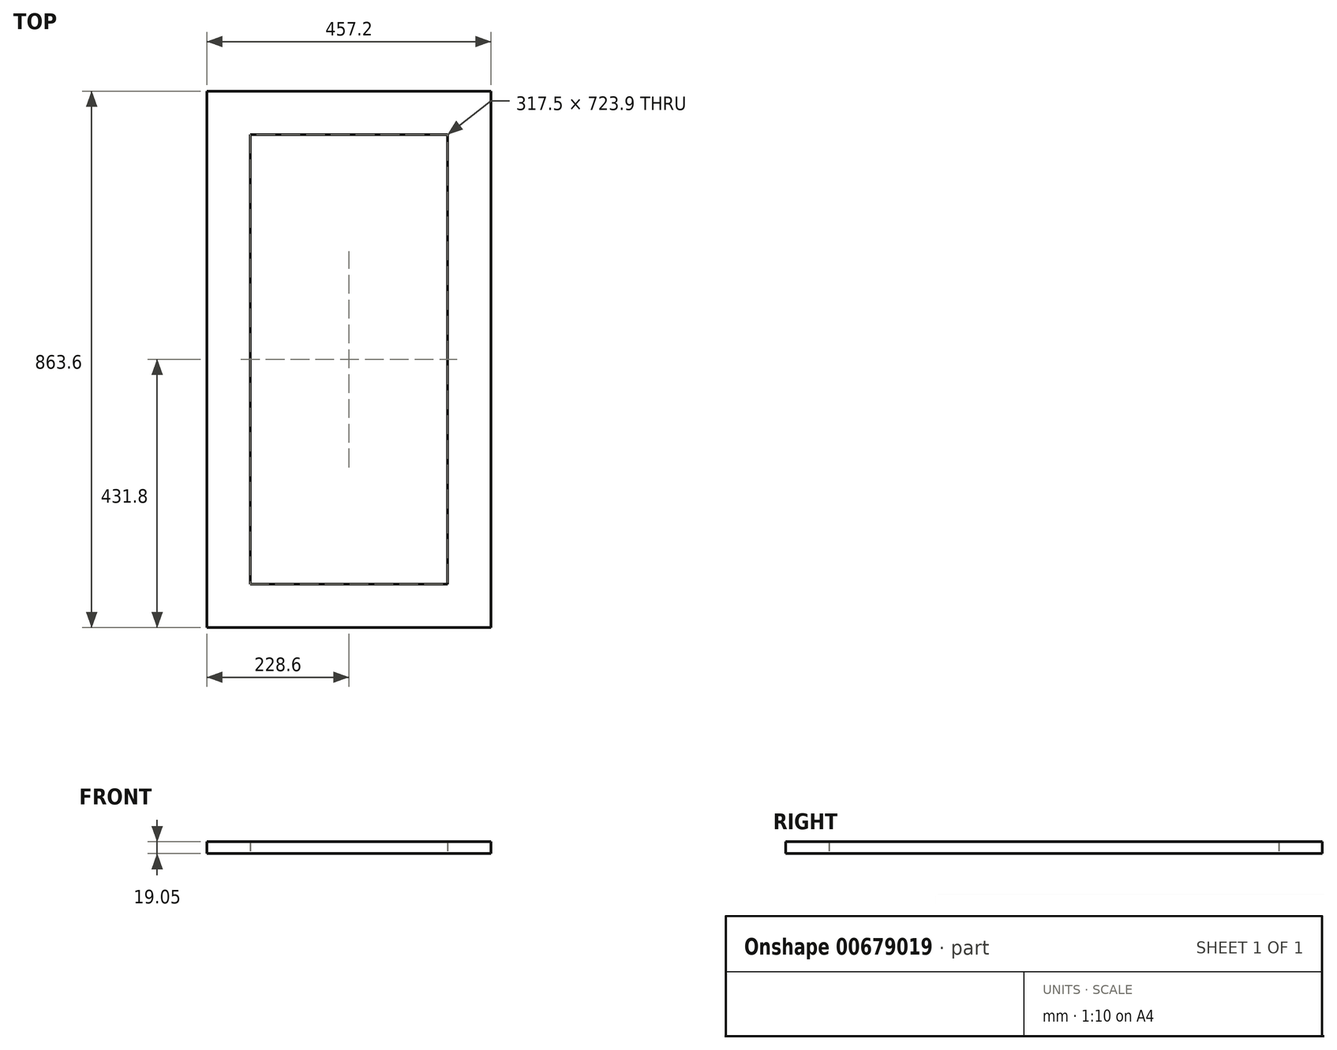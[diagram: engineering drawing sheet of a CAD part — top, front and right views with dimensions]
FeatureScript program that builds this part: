
annotation { "Feature Type Name" : "Feature", "Feature Type Description" : "" }
export const myFeature = defineFeature(function(context is Context, id is Id, definition is map)
    precondition{}
    {
        {
            var Q0;
            Q0=qCreatedBy(makeId("Top.planeOp"),FACE);
            var sketch = newSketch(context, id + "F0", { "sketchPlane" : qUnion([Q0])});
            skLineSegment(sketch, "E0.bottom", {"start": v(228.6, 431.8) * mm, "end": v(-228.6, 431.8) * mm});
            skLineSegment(sketch, "E0.top", {"start": v(228.6, -431.8) * mm, "end": v(-228.6, -431.8) * mm});
            skLineSegment(sketch, "E0.left", {"start": v(228.6, 431.8) * mm, "end": v(228.6, -431.8) * mm});
            skLineSegment(sketch, "E0.right", {"start": v(-228.6, 431.8) * mm, "end": v(-228.6, -431.8) * mm});
            skPoint(sketch, "E0.middle", {"position": v(0, 0) * mm});
            skLineSegment(sketch, "E1.bottom", {"start": v(158.75, 361.95) * mm, "end": v(-158.75, 361.95) * mm});
            skLineSegment(sketch, "E1.top", {"start": v(158.75, -361.95) * mm, "end": v(-158.75, -361.95) * mm});
            skLineSegment(sketch, "E1.left", {"start": v(158.75, 361.95) * mm, "end": v(158.75, -361.95) * mm});
            skLineSegment(sketch, "E1.right", {"start": v(-158.75, 361.95) * mm, "end": v(-158.75, -361.95) * mm});
            skSolve(sketch);
        }
        {
            var Q0;
            Q0=makeQuery(id+"F0.imprint","IMPRINT",FACE,{"disambiguationData":[TD([[makeQuery(id+"F0.imprint","IMPRINT",EDGE,{"derivedFrom":sQuery(id+"F0.wireOp",EDGE,"E0.bottom")}),1.0]])]});
            extrude(context, id + "F1", {"entities" : qUnion([Q0]), "depth" : 19.05 * mm, "offsetDistance" : 25.4 * mm});
        }
    });
